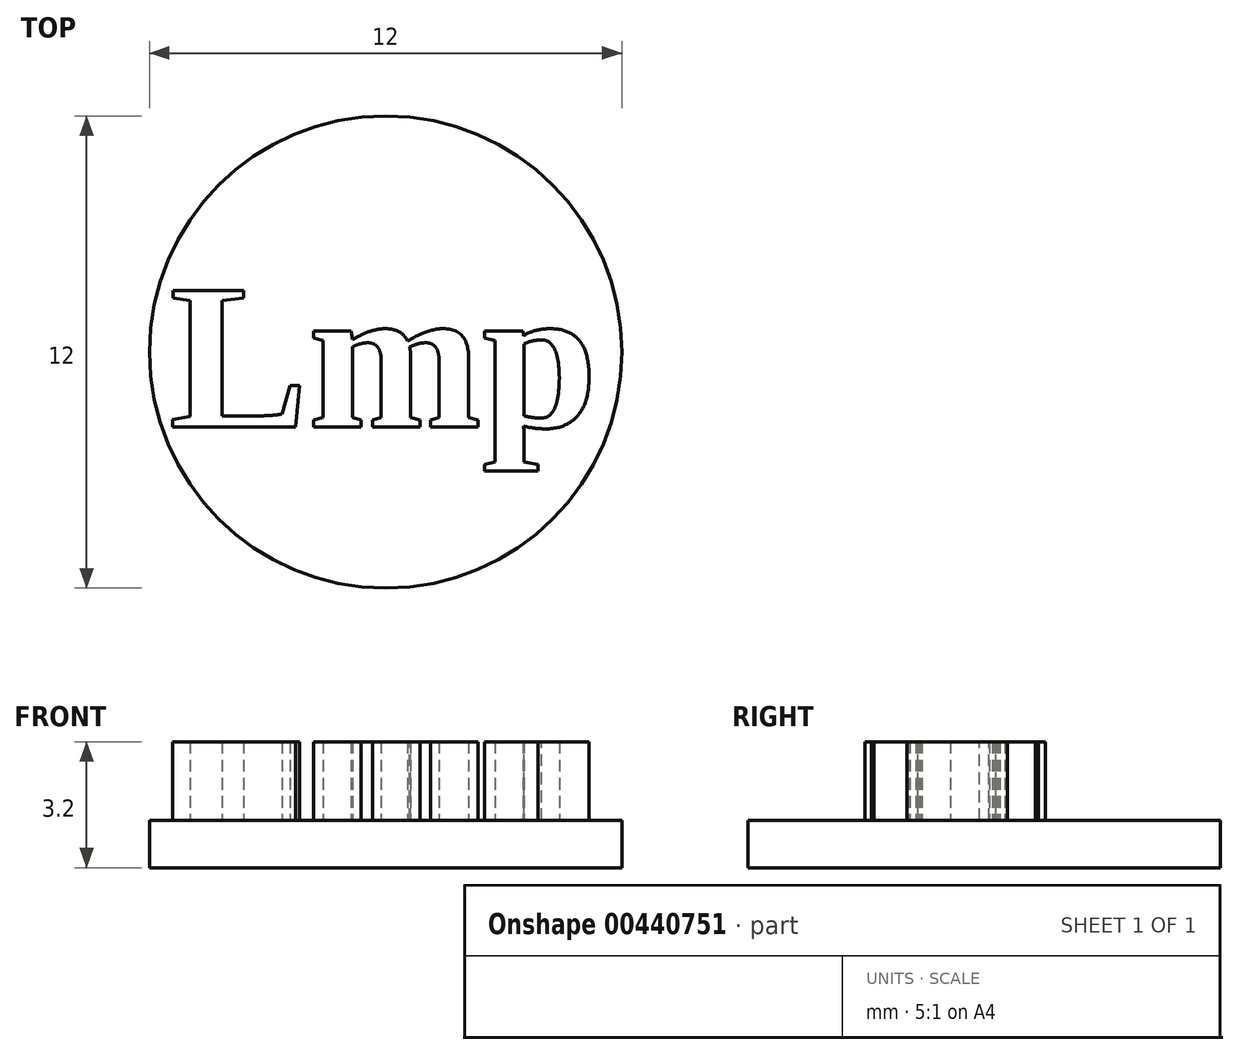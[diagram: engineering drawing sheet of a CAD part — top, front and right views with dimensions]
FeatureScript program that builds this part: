
annotation { "Feature Type Name" : "Feature", "Feature Type Description" : "" }
export const myFeature = defineFeature(function(context is Context, id is Id, definition is map)
    precondition{}
    {
        {
            var Q0;
            Q0=qCreatedBy(makeId("Top.planeOp"),FACE);
            var sketch = newSketch(context, id + "F0", { "sketchPlane" : qUnion([Q0])});
            skCircle(sketch, "E0", {"center": v(0, 0) * mm, "radius": 6 * mm});
            skSolve(sketch);
        }
        {
            var Q0;
            Q0 = qSketchRegion(id + "F0", true);
            extrude(context, id + "F1", {"entities" : qUnion([Q0]), "depth" : 1.2 * mm});
        }
        {
            var Q0;
            Q0=makeQuery(id+"F1.opExtrude","CAP_FACE",FACE,{"disambiguationData":[OSD([sQuery(id+"F0.wireOp",EDGE,"E0")])],"isStart":false});
            var sketch = newSketch(context, id + "F2", { "sketchPlane" : qUnion([Q0])});
            skText(sketch, "E1", { "text": "Lmp", "fontName": "Tinos-Bold.ttf"});
            skPoint(sketch, "E2", {"position": v(0, 0) * mm});
            const initialGuessF2  = {"E1": [-0.0055, -0.0019, 1, 0, 0.00381]};
            skSetInitialGuess(sketch, initialGuessF2);
            skSolve(sketch);
        }
        {
            var Q0;
            Q0 = qSketchRegion(id + "F2", true);
            extrude(context, id + "F3", {"entities" : qUnion([Q0]), "operationType" : NewBodyOperationType.ADD, "depth" : 2 * mm});
        }
    });
